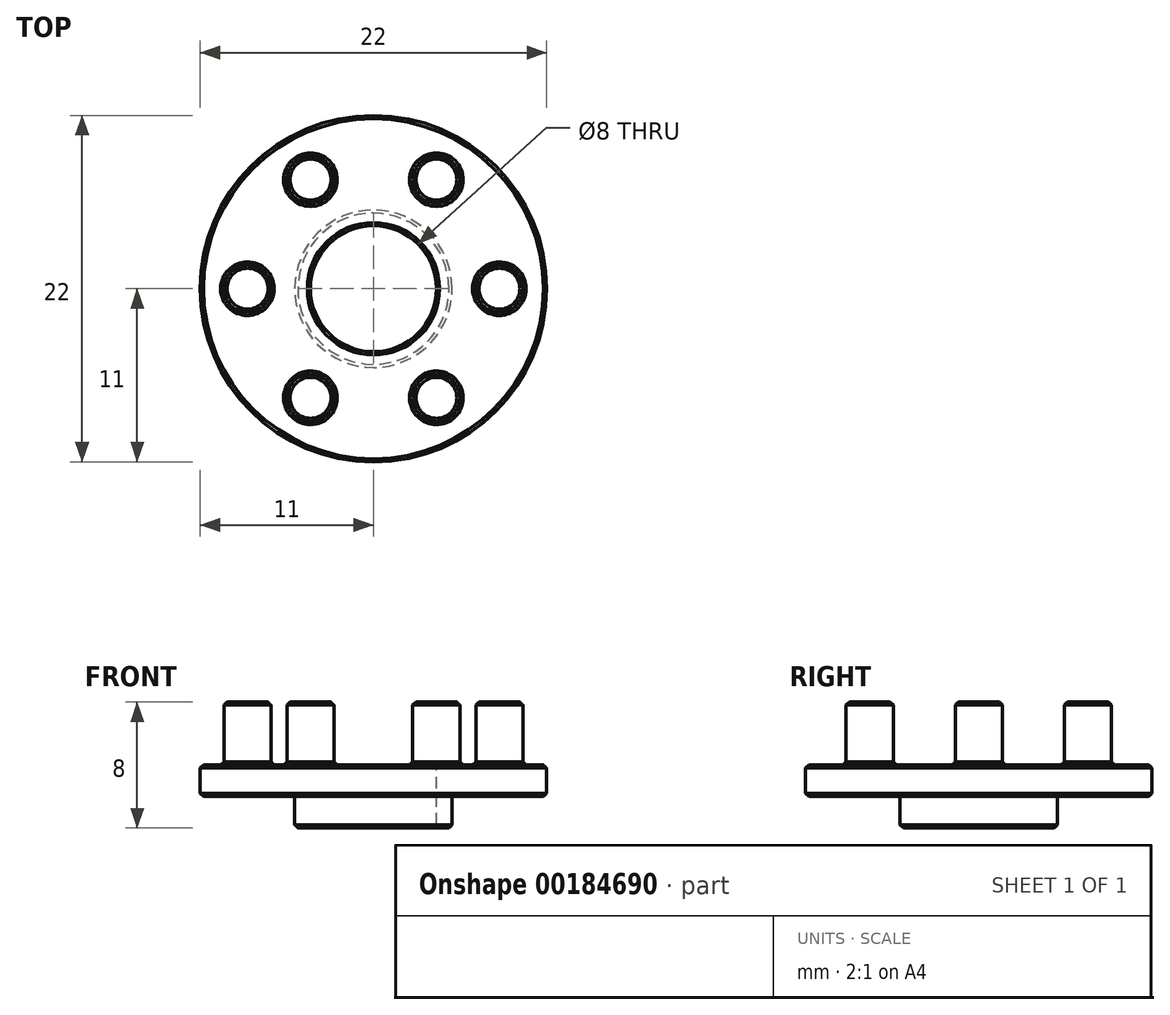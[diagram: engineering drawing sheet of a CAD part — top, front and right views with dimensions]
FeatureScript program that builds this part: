
annotation { "Feature Type Name" : "Feature", "Feature Type Description" : "" }
export const myFeature = defineFeature(function(context is Context, id is Id, definition is map)
    precondition{}
    {
        {
            var Q0;
            Q0=qCreatedBy(makeId("Top.planeOp"),FACE);
            var sketch = newSketch(context, id + "F0", { "sketchPlane" : qUnion([Q0])});
            skCircle(sketch, "E0", {"center": v(-8, 0) * mm, "radius": 1.5 * mm});
            skCircle(sketch, "E1.1.0", {"center": v(-4, -6.93) * mm, "radius": 1.5 * mm});
            skCircle(sketch, "E1.2.0", {"center": v(4, -6.93) * mm, "radius": 1.5 * mm});
            skCircle(sketch, "E1.3.0", {"center": v(8, 0) * mm, "radius": 1.5 * mm});
            skCircle(sketch, "E1.4.0", {"center": v(4, 6.93) * mm, "radius": 1.5 * mm});
            skCircle(sketch, "E1.5.0", {"center": v(-4, 6.93) * mm, "radius": 1.5 * mm});
            skPoint(sketch, "E1.center", {"position": v(0, 0) * mm});
            skCircle(sketch, "E2", {"center": v(0, 0) * mm, "radius": 4 * mm});
            skCircle(sketch, "E3", {"center": v(0, 0) * mm, "radius": 11 * mm});
            skSolve(sketch);
        }
        {
            var Q0;
            Q0=makeQuery(id+"F0.imprint","IMPRINT",FACE,{"disambiguationData":[TD([[makeQuery(id+"F0.imprint","IMPRINT",EDGE,{"derivedFrom":sQuery(id+"F0.wireOp",EDGE,"E0")}),1.0]])]});
            var Q1;
            Q1=makeQuery(id+"F0.imprint","IMPRINT",FACE,{"disambiguationData":[TD([[makeQuery(id+"F0.imprint","IMPRINT",EDGE,{"derivedFrom":sQuery(id+"F0.wireOp",EDGE,"E1.5.0")}),1.0]])]});
            var Q2;
            Q2=makeQuery(id+"F0.imprint","IMPRINT",FACE,{"disambiguationData":[TD([[makeQuery(id+"F0.imprint","IMPRINT",EDGE,{"derivedFrom":sQuery(id+"F0.wireOp",EDGE,"E1.4.0")}),1.0]])]});
            var Q3;
            Q3=makeQuery(id+"F0.imprint","IMPRINT",FACE,{"disambiguationData":[TD([[makeQuery(id+"F0.imprint","IMPRINT",EDGE,{"derivedFrom":sQuery(id+"F0.wireOp",EDGE,"E1.3.0")}),1.0]])]});
            var Q4;
            Q4=makeQuery(id+"F0.imprint","IMPRINT",FACE,{"disambiguationData":[TD([[makeQuery(id+"F0.imprint","IMPRINT",EDGE,{"derivedFrom":sQuery(id+"F0.wireOp",EDGE,"E1.2.0")}),1.0]])]});
            var Q5;
            Q5=makeQuery(id+"F0.imprint","IMPRINT",FACE,{"disambiguationData":[TD([[makeQuery(id+"F0.imprint","IMPRINT",EDGE,{"derivedFrom":sQuery(id+"F0.wireOp",EDGE,"E1.1.0")}),1.0]])]});
            extrude(context, id + "F1", {"entities" : qUnion([Q0, Q1, Q2, Q3, Q4, Q5]), "depth" : 4 * mm});
        }
        {
            var Q0;
            Q0=makeQuery(id+"F0.imprint","IMPRINT",FACE,{"disambiguationData":[TD([[makeQuery(id+"F0.imprint","IMPRINT",EDGE,{"derivedFrom":sQuery(id+"F0.wireOp",EDGE,"E0")}),-1.0]])]});
            var Q1;
            Q1=makeQuery(id+"F0.imprint","IMPRINT",FACE,{"disambiguationData":[TD([[makeQuery(id+"F0.imprint","IMPRINT",EDGE,{"derivedFrom":sQuery(id+"F0.wireOp",EDGE,"E1.2.0")}),1.0]])]});
            var Q2;
            Q2=makeQuery(id+"F0.imprint","IMPRINT",FACE,{"disambiguationData":[TD([[makeQuery(id+"F0.imprint","IMPRINT",EDGE,{"derivedFrom":sQuery(id+"F0.wireOp",EDGE,"E1.3.0")}),1.0]])]});
            var Q3;
            Q3=makeQuery(id+"F0.imprint","IMPRINT",FACE,{"disambiguationData":[TD([[makeQuery(id+"F0.imprint","IMPRINT",EDGE,{"derivedFrom":sQuery(id+"F0.wireOp",EDGE,"E1.4.0")}),1.0]])]});
            var Q4;
            Q4=makeQuery(id+"F0.imprint","IMPRINT",FACE,{"disambiguationData":[TD([[makeQuery(id+"F0.imprint","IMPRINT",EDGE,{"derivedFrom":sQuery(id+"F0.wireOp",EDGE,"E1.5.0")}),1.0]])]});
            var Q5;
            Q5=makeQuery(id+"F0.imprint","IMPRINT",FACE,{"disambiguationData":[TD([[makeQuery(id+"F0.imprint","IMPRINT",EDGE,{"derivedFrom":sQuery(id+"F0.wireOp",EDGE,"E0")}),1.0]])]});
            var Q6;
            Q6=makeQuery(id+"F0.imprint","IMPRINT",FACE,{"disambiguationData":[TD([[makeQuery(id+"F0.imprint","IMPRINT",EDGE,{"derivedFrom":sQuery(id+"F0.wireOp",EDGE,"E1.1.0")}),1.0]])]});
            extrude(context, id + "F2", {"entities" : qUnion([Q0, Q1, Q2, Q3, Q4, Q5, Q6]), "operationType" : NewBodyOperationType.ADD, "oppositeDirection" : true, "depth" : 2 * mm});
        }
        {
            var Q0;
            Q0=makeQuery(id+"F2.opExtrude","CAP_FACE",FACE,{"disambiguationData":[OSD([sQuery(id+"F0.wireOp",EDGE,"E2"),sQuery(id+"F0.wireOp",EDGE,"E3")])],"isStart":false});
            var sketch = newSketch(context, id + "F3", { "sketchPlane" : qUnion([Q0])});
            skCircle(sketch, "E4", {"center": v(0, 0) * mm, "radius": 5 * mm});
            skCircle(sketch, "E5", {"center": v(0, 0) * mm, "radius": 4 * mm});
            skSolve(sketch);
        }
        {
            var Q0;
            Q0=makeQuery(id+"F3.imprint","IMPRINT",FACE,{"disambiguationData":[TD([[makeQuery(id+"F3.imprint","IMPRINT",EDGE,{"derivedFrom":sQuery(id+"F3.wireOp",EDGE,"E4")}),1.0]])]});
            extrude(context, id + "F4", {"entities" : qUnion([Q0]), "operationType" : NewBodyOperationType.ADD, "depth" : 2 * mm});
        }
        {
            var Q0;
            Q0=makeQuery(id+"F2.opExtrude","CAP_FACE",FACE,{"disambiguationData":[OSD([sQuery(id+"F0.wireOp",EDGE,"E2"),sQuery(id+"F0.wireOp",EDGE,"E3")])],"isStart":true});
            var Q1;
            Q1=makeQuery(id+"F1.opExtrude","CAP_FACE",FACE,{"disambiguationData":[OSD([sQuery(id+"F0.wireOp",EDGE,"E1.3.0")])],"isStart":false});
            var Q2;
            Q2=makeQuery(id+"F1.opExtrude","CAP_FACE",FACE,{"disambiguationData":[OSD([sQuery(id+"F0.wireOp",EDGE,"E1.2.0")])],"isStart":false});
            var Q3;
            Q3=makeQuery(id+"F1.opExtrude","CAP_FACE",FACE,{"disambiguationData":[OSD([sQuery(id+"F0.wireOp",EDGE,"E1.1.0")])],"isStart":false});
            var Q4;
            Q4=makeQuery(id+"F1.opExtrude","CAP_FACE",FACE,{"disambiguationData":[OSD([sQuery(id+"F0.wireOp",EDGE,"E0")])],"isStart":false});
            var Q5;
            Q5=makeQuery(id+"F1.opExtrude","CAP_FACE",FACE,{"disambiguationData":[OSD([sQuery(id+"F0.wireOp",EDGE,"E1.5.0")])],"isStart":false});
            var Q6;
            Q6=makeQuery(id+"F1.opExtrude","CAP_FACE",FACE,{"disambiguationData":[OSD([sQuery(id+"F0.wireOp",EDGE,"E1.4.0")])],"isStart":false});
            var Q7;
            Q7=makeQuery(id+"F4.opExtrude","CAP_EDGE",EDGE,{"disambiguationData":[OSD([sQuery(id+"F3.wireOp",EDGE,"E5")])],"isStart":false});
            var Q8;
            Q8=makeQuery(id+"F4.opExtrude","CAP_EDGE",EDGE,{"disambiguationData":[OSD([sQuery(id+"F3.wireOp",EDGE,"E4")])],"isStart":false});
            var Q9;
            Q9=makeQuery(id+"F4.opExtrude","CAP_EDGE",EDGE,{"disambiguationData":[OSD([sQuery(id+"F3.wireOp",EDGE,"E4")])],"isStart":true});
            var Q10;
            Q10=makeQuery(id+"F2.opExtrude","CAP_EDGE",EDGE,{"disambiguationData":[OSD([sQuery(id+"F0.wireOp",EDGE,"E3")])],"isStart":false});
            chamfer(context, id + "F5", {"entities" : qUnion([Q0, Q1, Q2, Q3, Q4, Q5, Q6, Q7, Q8, Q9, Q10]), "width" : 0.2 * mm, "tangentPropagation" : true});
        }
    });
